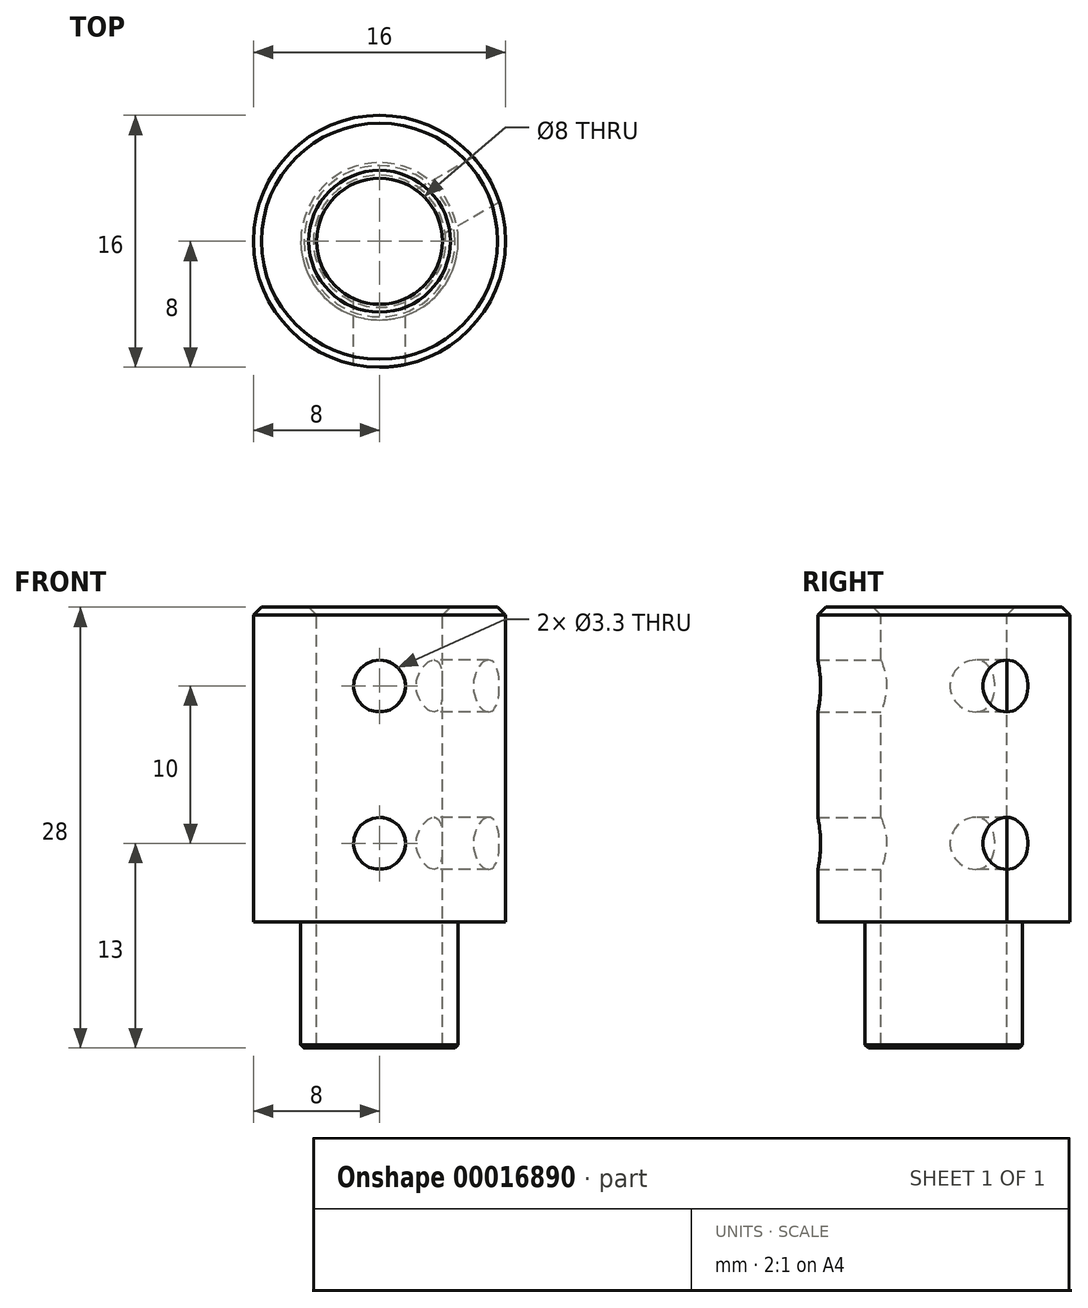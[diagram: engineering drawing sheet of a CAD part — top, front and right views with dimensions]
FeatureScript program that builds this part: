
annotation { "Feature Type Name" : "Feature", "Feature Type Description" : "" }
export const myFeature = defineFeature(function(context is Context, id is Id, definition is map)
    precondition{}
    {
        {
            var Q0;
            Q0=qCreatedBy(makeId("Front.planeOp"),FACE);
            var sketch = newSketch(context, id + "F0", { "sketchPlane" : qUnion([Q0])});
            skLineSegment(sketch, "E0", {"start": v(0, 10.44) * mm, "end": v(0, 0) * mm, "construction": true});
            skLineSegment(sketch, "E1", {"start": v(4, -28) * mm, "end": v(4, 0) * mm});
            skLineSegment(sketch, "E2", {"start": v(4, 0) * mm, "end": v(8, 0) * mm});
            skLineSegment(sketch, "E3", {"start": v(8, 0) * mm, "end": v(8, -20) * mm});
            skLineSegment(sketch, "E4", {"start": v(8, -20) * mm, "end": v(5, -20) * mm});
            skLineSegment(sketch, "E5", {"start": v(5, -20) * mm, "end": v(5, -28) * mm});
            skLineSegment(sketch, "E6", {"start": v(5, -28) * mm, "end": v(4, -28) * mm});
            skLineSegment(sketch, "E7.MirrorCS", {"start": v(-4, 0) * mm, "end": v(-8, 0) * mm, "construction": true});
            skLineSegment(sketch, "E8.MirrorCS", {"start": v(-8, -20) * mm, "end": v(-5, -20) * mm, "construction": true});
            skLineSegment(sketch, "E9.MirrorCS", {"start": v(-5, -28) * mm, "end": v(-4, -28) * mm, "construction": true});
            skLineSegment(sketch, "E10.MirrorCS", {"start": v(-8, 0) * mm, "end": v(-8, -20) * mm, "construction": true});
            skLineSegment(sketch, "E11.MirrorCS", {"start": v(-4, -28) * mm, "end": v(-4, 0) * mm, "construction": true});
            skLineSegment(sketch, "E12.MirrorCS", {"start": v(-5, -20) * mm, "end": v(-5, -28) * mm, "construction": true});
            skCircle(sketch, "E13", {"center": v(0, -5) * mm, "radius": 1.65 * mm, "construction": true});
            skCircle(sketch, "E14", {"center": v(0, -15) * mm, "radius": 1.65 * mm, "construction": true});
            skLineSegment(sketch, "E15", {"start": v(0, 0) * mm, "end": v(0, -5) * mm, "construction": true});
            skLineSegment(sketch, "E16", {"start": v(0, -5) * mm, "end": v(0, -15) * mm, "construction": true});
            skLineSegment(sketch, "E17", {"start": v(0, -15) * mm, "end": v(0, -20) * mm, "construction": true});
            skSolve(sketch);
        }
        {
            var Q0;
            Q0 = qSketchRegion(id + "F0", true);
            var Q1;
            Q1=sQuery(id+"F0.wireOp",EDGE,"E0");
            revolve(context, id + "F1", {"entities" : qUnion([Q0]), "axis" : qUnion([Q1]), "revolveType" : RevolveType.FULL});
        }
        {
            var Q0;
            Q0=makeQuery(id+"F1.opRevolve","SWEPT_EDGE",EDGE,{"disambiguationData":[OSD([sQuery(id+"F0.wireOp",EDGE,"E1"),sQuery(id+"F0.wireOp",EDGE,"E2")])]});
            var Q1;
            Q1=makeQuery(id+"F1.opRevolve","SWEPT_EDGE",EDGE,{"disambiguationData":[OSD([sQuery(id+"F0.wireOp",EDGE,"E2"),sQuery(id+"F0.wireOp",EDGE,"E3")])]});
            chamfer(context, id + "F2", {"entities" : qUnion([Q0, Q1]), "width" : .5 * mm, "tangentPropagation" : true});
        }
        {
            var Q0;
            Q0=makeQuery(id+"F1.opRevolve","SWEPT_FACE",FACE,{"disambiguationData":[OSD([sQuery(id+"F0.wireOp",EDGE,"E6")])]});
            chamfer(context, id + "F3", {"entities" : qUnion([Q0]), "width" : .2 * mm, "tangentPropagation" : true});
        }
        {
            var Q0;
            Q0=qCreatedBy(makeId("Front.planeOp"),FACE);
            var sketch = newSketch(context, id + "F4", { "sketchPlane" : qUnion([Q0])});
            skCircle(sketch, "E18.0", {"center": v(0, -5) * mm, "radius": 1.65 * mm});
            skCircle(sketch, "E18.1", {"center": v(0, -15) * mm, "radius": 1.65 * mm});
            skSolve(sketch);
        }
        {
            var Q0;
            Q0 = qSketchRegion(id + "F4", true);
            extrude(context, id + "F5", {"entities" : qUnion([Q0]), "operationType" : NewBodyOperationType.REMOVE, "endBound" : BoundingType.THROUGH_ALL, "depth" : 25 * mm});
        }
        {
            var Q0;
            Q0=makeQuery(id+"F5.boolean.opBoolean","COPY",FACE,{"derivedFrom":makeQuery(id+"F5.opExtrude","SWEPT_FACE",FACE,{"disambiguationData":[OSD([sQuery(id+"F4.wireOp",EDGE,"E18.0")])]})});
            var Q1;
            Q1=makeQuery(id+"F5.boolean.opBoolean","COPY",FACE,{"derivedFrom":makeQuery(id+"F5.opExtrude","SWEPT_FACE",FACE,{"disambiguationData":[OSD([sQuery(id+"F4.wireOp",EDGE,"E18.1")])]})});
            var Q2;
            Q2=makeQuery(id+"F1.opRevolve","SWEPT_FACE",FACE,{"disambiguationData":[OSD([sQuery(id+"F0.wireOp",EDGE,"E1")])]});
            circularPattern(context, id + "F6", {"faces" : qUnion([Q0, Q1]), "axis" : qUnion([Q2]), "angle" : 120 * degree, "instanceCount" : 2, "oppositeDirection" : true, "patternType" : PatternType.FACE});
        }
    });
